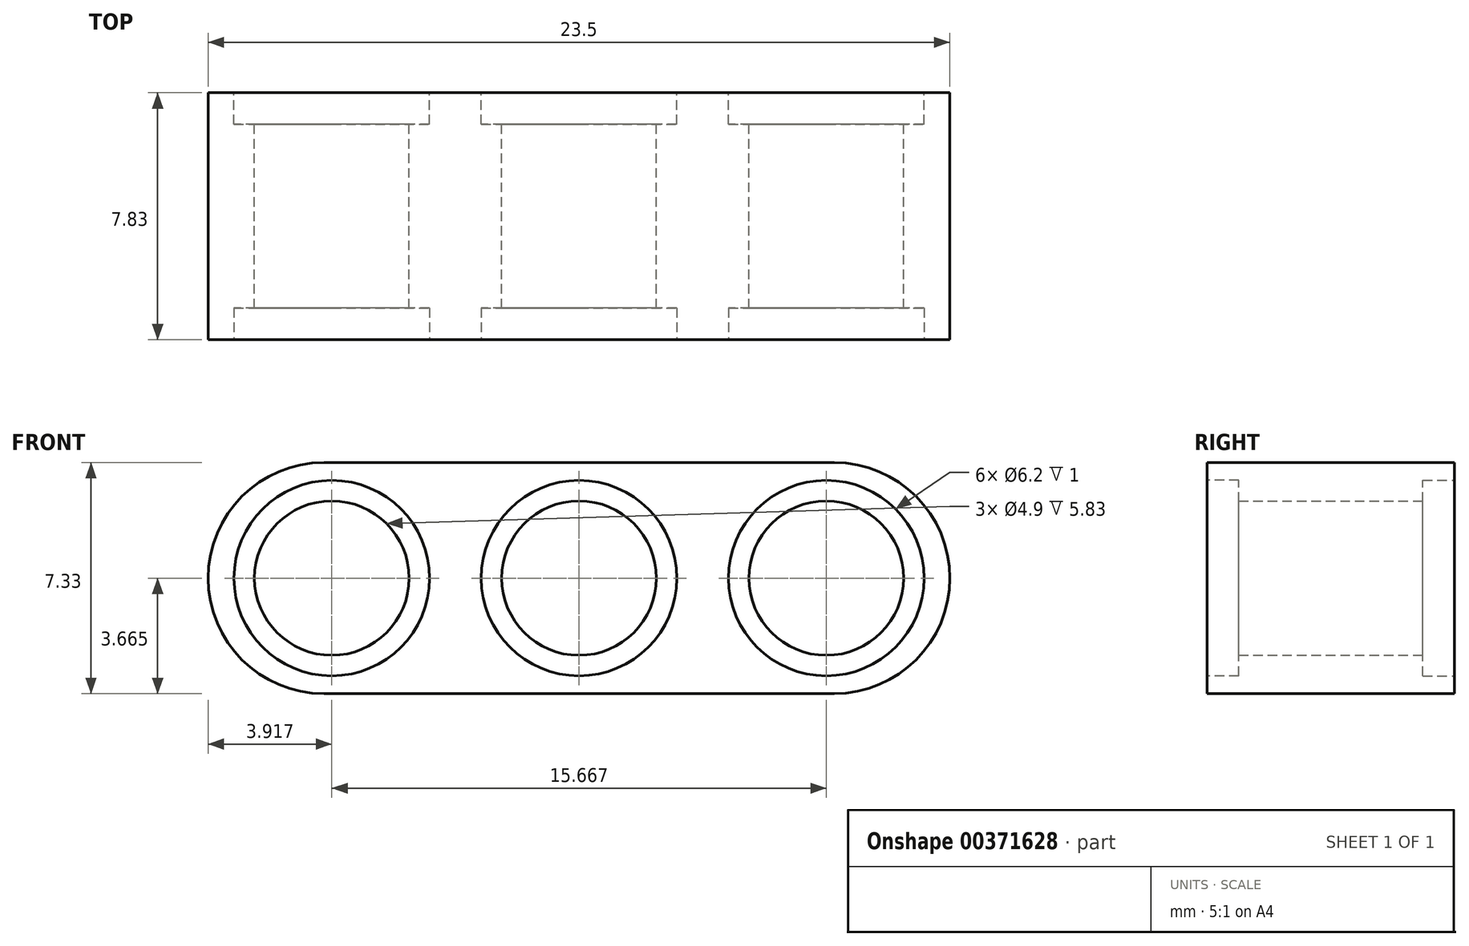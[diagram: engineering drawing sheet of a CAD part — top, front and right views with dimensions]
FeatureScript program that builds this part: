
annotation { "Feature Type Name" : "Feature", "Feature Type Description" : "" }
export const myFeature = defineFeature(function(context is Context, id is Id, definition is map)
    precondition{}
    {
        {
            var Q0;
            Q0=qCreatedBy(makeId("Front.planeOp"),FACE);
            var sketch = newSketch(context, id + "F0", { "sketchPlane" : qUnion([Q0])});
            skLineSegment(sketch, "E0", {"start": v(3.67, 0) * mm, "end": v(19.83, 0) * mm});
            skLineSegment(sketch, "E1", {"start": v(23.5, 0) * mm, "end": v(15.67, 0) * mm, "construction": true});
            skLineSegment(sketch, "E2", {"start": v(23.5, 3.67) * mm, "end": v(23.5, 3.67) * mm});
            skLineSegment(sketch, "E3", {"start": v(15.67, 0) * mm, "end": v(7.83, 0) * mm, "construction": true});
            skLineSegment(sketch, "E4", {"start": v(0, 3.67) * mm, "end": v(23.5, 3.67) * mm, "construction": true});
            skLineSegment(sketch, "E5", {"start": v(19.83, 7.33) * mm, "end": v(15.67, 7.33) * mm});
            skLineSegment(sketch, "E6", {"start": v(15.67, 7.33) * mm, "end": v(7.83, 7.33) * mm});
            skLineSegment(sketch, "E7", {"start": v(7.83, 7.33) * mm, "end": v(3.67, 7.33) * mm});
            skLineSegment(sketch, "E8", {"start": v(0, 3.66) * mm, "end": v(0, 3.67) * mm});
            skLineSegment(sketch, "E9", {"start": v(15.67, 7.33) * mm, "end": v(15.67, 0) * mm, "construction": true});
            skLineSegment(sketch, "E10", {"start": v(7.83, 0) * mm, "end": v(7.83, 7.33) * mm, "construction": true});
            skLineSegment(sketch, "E11", {"start": v(3.92, 0) * mm, "end": v(3.92, 7.33) * mm, "construction": true});
            skLineSegment(sketch, "E12", {"start": v(11.75, 7.33) * mm, "end": v(11.75, 0) * mm, "construction": true});
            skLineSegment(sketch, "E13", {"start": v(19.58, 7.33) * mm, "end": v(19.58, 0) * mm, "construction": true});
            skPoint(sketch, "E14.visualSharp", {"position": v(0, 7.33) * mm});
            skArc(sketch, "E14.filletArc", {"start": v(3.67, 7.33) * mm, "mid": v(1.07, 6.26) * mm, "end": v(0, 3.66) * mm});
            skPoint(sketch, "E15.visualSharp", {"position": v(0, 0) * mm});
            skArc(sketch, "E15.filletArc", {"start": v(0, 3.67) * mm, "mid": v(1.07, 1.07) * mm, "end": v(3.67, 0) * mm});
            skPoint(sketch, "E16.visualSharp", {"position": v(23.5, 7.33) * mm});
            skArc(sketch, "E16.filletArc", {"start": v(23.5, 3.67) * mm, "mid": v(22.43, 6.26) * mm, "end": v(19.83, 7.33) * mm});
            skPoint(sketch, "E17.visualSharp", {"position": v(23.5, 0) * mm});
            skArc(sketch, "E17.filletArc", {"start": v(19.83, 0) * mm, "mid": v(22.43, 1.07) * mm, "end": v(23.5, 3.67) * mm});
            skCircle(sketch, "E18", {"center": v(3.92, 3.67) * mm, "radius": 2.45 * mm});
            skCircle(sketch, "E19", {"center": v(19.58, 3.67) * mm, "radius": 2.45 * mm});
            skCircle(sketch, "E20", {"center": v(11.75, 3.67) * mm, "radius": 2.45 * mm});
            skArc(sketch, "E21", {"start": v(5.5, 6.33) * mm, "mid": v(0.82, 3.67) * mm, "end": v(5.5, 1) * mm});
            skArc(sketch, "E22", {"start": v(5.5, 1) * mm, "mid": v(7.02, 3.67) * mm, "end": v(5.5, 6.33) * mm});
            skArc(sketch, "E23", {"start": v(10.17, 6.33) * mm, "mid": v(8.65, 3.67) * mm, "end": v(10.17, 1) * mm});
            skArc(sketch, "E24", {"start": v(10.17, 1) * mm, "mid": v(11.75, 0.56) * mm, "end": v(13.33, 1) * mm});
            skArc(sketch, "E25", {"start": v(13.33, 6.33) * mm, "mid": v(11.75, 6.77) * mm, "end": v(10.17, 6.33) * mm});
            skArc(sketch, "E26", {"start": v(13.33, 1) * mm, "mid": v(14.85, 3.67) * mm, "end": v(13.33, 6.33) * mm});
            skArc(sketch, "E27", {"start": v(18, 6.33) * mm, "mid": v(16.48, 3.67) * mm, "end": v(18, 1) * mm});
            skArc(sketch, "E28", {"start": v(18, 1) * mm, "mid": v(22.68, 3.67) * mm, "end": v(18, 6.33) * mm});
            skSolve(sketch);
        }
        {
            var Q0;
            Q0=makeQuery(id+"F0.imprint","IMPRINT",FACE,{"disambiguationData":[TD([[makeQuery(id+"F0.imprint","IMPRINT",EDGE,{"derivedFrom":sQuery(id+"F0.wireOp",EDGE,"E0")}),1.0]])]});
            var Q1;
            Q1=makeQuery(id+"F0.imprint","IMPRINT",FACE,{"disambiguationData":[TD([[makeQuery(id+"F0.imprint","IMPRINT",EDGE,{"derivedFrom":sQuery(id+"F0.wireOp",EDGE,"E18")}),-1.0]])]});
            var Q2;
            Q2=makeQuery(id+"F0.imprint","IMPRINT",FACE,{"disambiguationData":[TD([[makeQuery(id+"F0.imprint","IMPRINT",EDGE,{"derivedFrom":sQuery(id+"F0.wireOp",EDGE,"E20")}),-1.0]])]});
            var Q3;
            Q3=makeQuery(id+"F0.imprint","IMPRINT",FACE,{"disambiguationData":[TD([[makeQuery(id+"F0.imprint","IMPRINT",EDGE,{"derivedFrom":sQuery(id+"F0.wireOp",EDGE,"E19")}),-1.0]])]});
            extrude(context, id + "F1", {"entities" : qUnion([Q0, Q1, Q2, Q3]), "depth" : 7.83 * mm});
        }
        {
            var Q0;
            Q0=makeQuery(id+"F0.imprint","IMPRINT",FACE,{"disambiguationData":[TD([[makeQuery(id+"F0.imprint","IMPRINT",EDGE,{"derivedFrom":sQuery(id+"F0.wireOp",EDGE,"E18")}),-1.0]])]});
            var Q1;
            Q1=makeQuery(id+"F0.imprint","IMPRINT",FACE,{"disambiguationData":[TD([[makeQuery(id+"F0.imprint","IMPRINT",EDGE,{"derivedFrom":sQuery(id+"F0.wireOp",EDGE,"E20")}),-1.0]])]});
            var Q2;
            Q2=makeQuery(id+"F0.imprint","IMPRINT",FACE,{"disambiguationData":[TD([[makeQuery(id+"F0.imprint","IMPRINT",EDGE,{"derivedFrom":sQuery(id+"F0.wireOp",EDGE,"E19")}),-1.0]])]});
            extrude(context, id + "F2", {"entities" : qUnion([Q0, Q1, Q2]), "operationType" : NewBodyOperationType.REMOVE, "depth" : 1 * mm});
        }
        {
            var Q0;
            Q0=makeQuery(id+"F1.opExtrude","CAP_FACE",FACE,{"disambiguationData":[OSD([sQuery(id+"F0.wireOp",EDGE,"E0"),sQuery(id+"F0.wireOp",EDGE,"E5"),sQuery(id+"F0.wireOp",EDGE,"E6"),sQuery(id+"F0.wireOp",EDGE,"E7"),sQuery(id+"F0.wireOp",EDGE,"E14.filletArc"),sQuery(id+"F0.wireOp",EDGE,"E15.filletArc"),sQuery(id+"F0.wireOp",EDGE,"E16.filletArc"),sQuery(id+"F0.wireOp",EDGE,"E17.filletArc"),sQuery(id+"F0.wireOp",EDGE,"E18"),sQuery(id+"F0.wireOp",EDGE,"E19"),sQuery(id+"F0.wireOp",EDGE,"E20")])],"isStart":false});
            var sketch = newSketch(context, id + "F3", { "sketchPlane" : qUnion([Q0])});
            skCircle(sketch, "E29", {"center": v(3.92, 3.67) * mm, "radius": 3.1 * mm});
            skCircle(sketch, "E30", {"center": v(11.75, 3.67) * mm, "radius": 3.1 * mm});
            skCircle(sketch, "E31", {"center": v(19.58, 3.67) * mm, "radius": 3.1 * mm});
            skSolve(sketch);
        }
        {
            var Q0;
            Q0=makeQuery(id+"F3.imprint","IMPRINT",FACE,{"disambiguationData":[TD([[makeQuery(id+"F3.imprint","IMPRINT",EDGE,{"derivedFrom":sQuery(id+"F3.wireOp",EDGE,"E29")}),1.0]])]});
            var Q1;
            Q1=makeQuery(id+"F3.imprint","IMPRINT",FACE,{"disambiguationData":[TD([[makeQuery(id+"F3.imprint","IMPRINT",EDGE,{"derivedFrom":sQuery(id+"F3.wireOp",EDGE,"E30")}),1.0]])]});
            var Q2;
            Q2=makeQuery(id+"F3.imprint","IMPRINT",FACE,{"disambiguationData":[TD([[makeQuery(id+"F3.imprint","IMPRINT",EDGE,{"derivedFrom":sQuery(id+"F3.wireOp",EDGE,"E31")}),1.0]])]});
            extrude(context, id + "F4", {"entities" : qUnion([Q0, Q1, Q2]), "operationType" : NewBodyOperationType.REMOVE, "oppositeDirection" : true, "depth" : 1 * mm});
        }
    });
